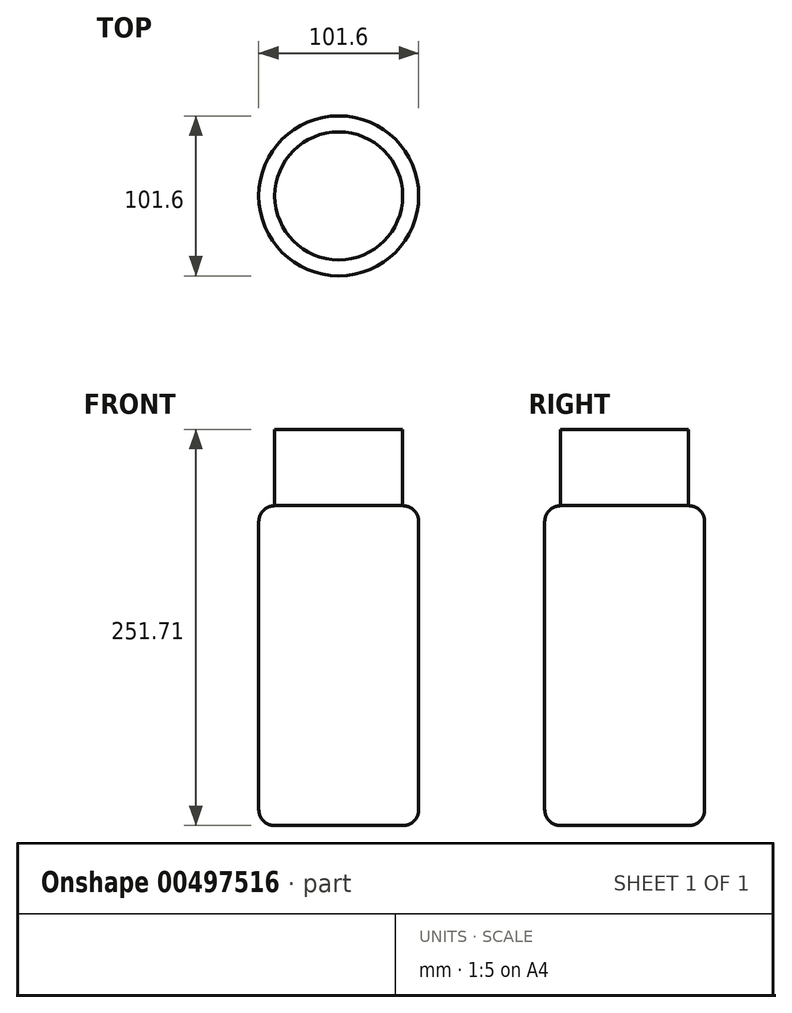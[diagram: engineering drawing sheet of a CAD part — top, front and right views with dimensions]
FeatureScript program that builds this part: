
annotation { "Feature Type Name" : "Feature", "Feature Type Description" : "" }
export const myFeature = defineFeature(function(context is Context, id is Id, definition is map)
    precondition{}
    {
        {
            var Q0;
            Q0=qCreatedBy(makeId("Top.planeOp"),FACE);
            var sketch = newSketch(context, id + "F0", { "sketchPlane" : qUnion([Q0])});
            skCircle(sketch, "E0", {"center": v(0, 0) * mm, "radius": 50.8 * mm});
            skSolve(sketch);
        }
        {
            var Q0;
            Q0=makeQuery(id+"F0.imprint","IMPRINT",FACE,{"disambiguationData":[TD([[makeQuery(id+"F0.imprint","IMPRINT",EDGE,{"derivedFrom":sQuery(id+"F0.wireOp",EDGE,"E0")}),1.0]])]});
            var Q1;
            Q1=sQuery(id+"F0.wireOp",EDGE,"E0");
            extrude(context, id + "F1", {"entities" : qUnion([Q0]), "surfaceEntities" : qUnion([Q1]), "depth" : 203.2 * mm});
        }
        {
            var Q0;
            Q0=makeQuery(id+"F1.opExtrude","CAP_FACE",FACE,{"disambiguationData":[OSD([sQuery(id+"F0.wireOp",EDGE,"E0")])],"isStart":true});
            var Q1;
            Q1=makeQuery(id+"F1.opExtrude","SWEPT_FACE",FACE,{"disambiguationData":[OSD([sQuery(id+"F0.wireOp",EDGE,"E0")])]});
            fillet(context, id + "F2", {"entities" : qUnion([Q0, Q1]), "radius" : 10.16 * mm, "tangentPropagation" : true, "allowEdgeOverflow" : false});
        }
        {
            var Q0;
            Q0=makeQuery(id+"F1.opExtrude","CAP_FACE",FACE,{"disambiguationData":[OSD([sQuery(id+"F0.wireOp",EDGE,"E0")])],"isStart":false});
            extrude(context, id + "F3", {"entities" : qUnion([Q0]), "operationType" : NewBodyOperationType.ADD, "depth" : 48.5 * mm});
        }
    });
